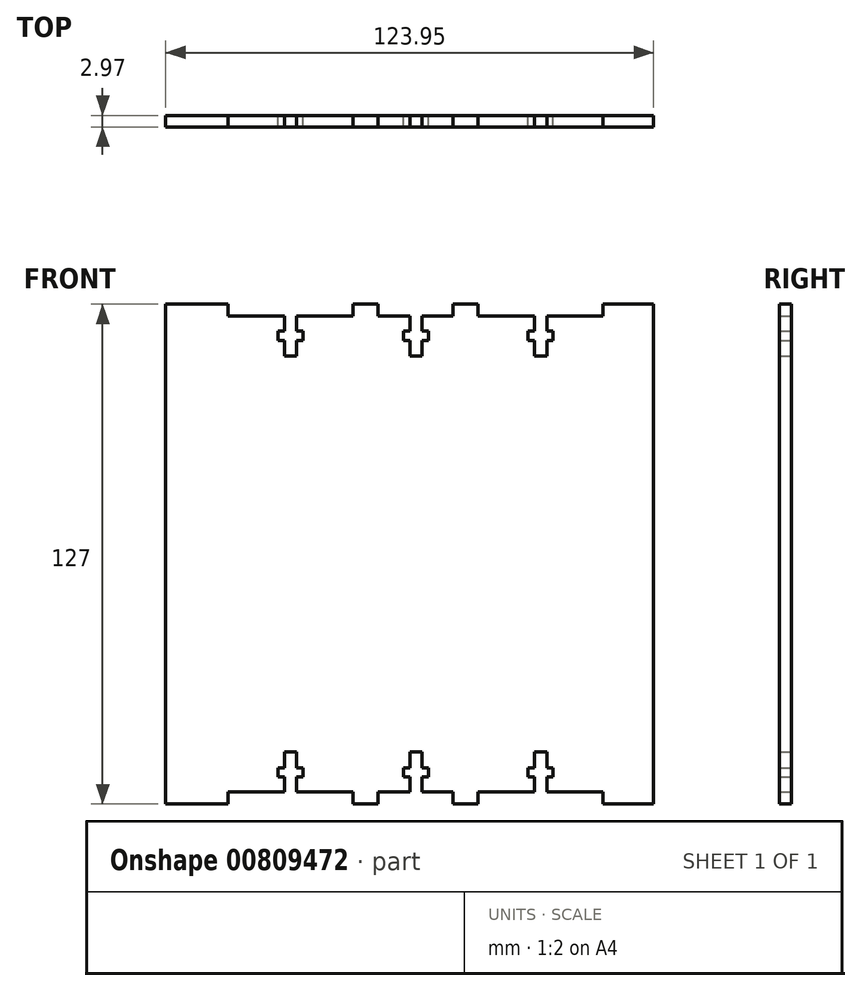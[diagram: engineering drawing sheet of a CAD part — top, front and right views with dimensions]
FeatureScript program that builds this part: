
annotation { "Feature Type Name" : "Feature", "Feature Type Description" : "" }
export const myFeature = defineFeature(function(context is Context, id is Id, definition is map)
    precondition{}
    {
        {
            var Q0;
            Q0=qCreatedBy(makeId("Front.planeOp"),FACE);
            var sketch = newSketch(context, id + "F0", { "sketchPlane" : qUnion([Q0])});
            skLineSegment(sketch, "E0.top", {"start": v(-63.5, -63.5) * mm, "end": v(-47.62, -63.5) * mm});
            skLineSegment(sketch, "E0.right", {"start": v(60.45, 0) * mm, "end": v(60.45, -63.5) * mm});
            skLineSegment(sketch, "E1", {"start": v(-60.45, 60.45) * mm, "end": v(-60.45, -67.28) * mm, "construction": true});
            skLineSegment(sketch, "E2", {"start": v(-66.3, -60.45) * mm, "end": v(-33.27, -60.45) * mm, "construction": true});
            skLineSegment(sketch, "E3", {"start": v(-47.62, -63.5) * mm, "end": v(-47.62, -60.45) * mm});
            skLineSegment(sketch, "E4", {"start": v(-15.88, -60.45) * mm, "end": v(-15.88, -63.5) * mm});
            skLineSegment(sketch, "E5", {"start": v(-9.53, -60.45) * mm, "end": v(-9.53, -63.5) * mm});
            skLineSegment(sketch, "E6.MirrorCS", {"start": v(9.53, -60.45) * mm, "end": v(9.53, -63.5) * mm});
            skLineSegment(sketch, "E7.MirrorCS", {"start": v(15.88, -60.45) * mm, "end": v(15.88, -63.5) * mm});
            skLineSegment(sketch, "E8.MirrorCS", {"start": v(47.62, -63.5) * mm, "end": v(47.62, -60.45) * mm});
            skLineSegment(sketch, "E9", {"start": v(-47.62, -60.45) * mm, "end": v(-33.27, -60.45) * mm});
            skLineSegment(sketch, "E10", {"start": v(-9.53, -60.45) * mm, "end": v(-1.44, -60.45) * mm});
            skLineSegment(sketch, "E11", {"start": v(15.88, -60.45) * mm, "end": v(30.16, -60.45) * mm});
            skLineSegment(sketch, "E12.trimOffspring", {"start": v(-15.88, -63.5) * mm, "end": v(-9.53, -63.5) * mm});
            skLineSegment(sketch, "E13.trimOffspring", {"start": v(-9.53, -60.45) * mm, "end": v(-1.44, -60.45) * mm, "construction": true});
            skLineSegment(sketch, "E14.trimOffspring", {"start": v(9.53, -63.5) * mm, "end": v(15.88, -63.5) * mm});
            skLineSegment(sketch, "E15.trimOffspring", {"start": v(47.62, -63.5) * mm, "end": v(60.45, -63.5) * mm});
            skLineSegment(sketch, "E16.trimOffspring", {"start": v(-63.5, -60.45) * mm, "end": v(-63.5, -63.5) * mm});
            skLineSegment(sketch, "E17", {"start": v(-63.5, -60.45) * mm, "end": v(-63.5, 0) * mm});
            skLineSegment(sketch, "E18", {"start": v(-63.5, 0) * mm, "end": v(60.45, 0) * mm});
            skLineSegment(sketch, "E19", {"start": v(-31.75, -61.85) * mm, "end": v(-31.75, 47.1) * mm, "construction": true});
            skLineSegment(sketch, "E20", {"start": v(31.75, -68.49) * mm, "end": v(31.75, 41.39) * mm, "construction": true});
            skLineSegment(sketch, "E21", {"start": v(-33.27, -60.45) * mm, "end": v(-33.27, -56.64) * mm});
            skLineSegment(sketch, "E22", {"start": v(-31.75, -50.3) * mm, "end": v(-33.27, -50.3) * mm});
            skLineSegment(sketch, "E23", {"start": v(-34.92, -54.26) * mm, "end": v(-34.92, -56.64) * mm});
            skLineSegment(sketch, "E24", {"start": v(-34.92, -56.64) * mm, "end": v(-33.27, -56.64) * mm});
            skLineSegment(sketch, "E25", {"start": v(-34.92, -54.26) * mm, "end": v(-33.27, -54.26) * mm});
            skLineSegment(sketch, "E26.trimOffspring", {"start": v(-33.27, -54.26) * mm, "end": v(-33.27, -50.3) * mm});
            skLineSegment(sketch, "E27.trimOffspring", {"start": v(-30.23, -60.45) * mm, "end": v(-15.88, -60.45) * mm, "construction": true});
            skLineSegment(sketch, "E28.trimOffspring", {"start": v(-30.23, -60.45) * mm, "end": v(-15.88, -60.45) * mm});
            skLineSegment(sketch, "E29.MirrorCS", {"start": v(-28.57, -54.26) * mm, "end": v(-30.23, -54.26) * mm});
            skLineSegment(sketch, "E30.MirrorCS", {"start": v(-28.57, -56.64) * mm, "end": v(-30.23, -56.64) * mm});
            skLineSegment(sketch, "E31.MirrorCS", {"start": v(-30.23, -60.45) * mm, "end": v(-30.23, -56.64) * mm});
            skLineSegment(sketch, "E32.MirrorCS", {"start": v(-30.23, -54.26) * mm, "end": v(-30.23, -50.3) * mm});
            skLineSegment(sketch, "E33.MirrorCS", {"start": v(-28.57, -54.26) * mm, "end": v(-28.57, -56.64) * mm});
            skLineSegment(sketch, "E34", {"start": v(-30.23, -50.3) * mm, "end": v(-31.75, -50.3) * mm});
            skLineSegment(sketch, "E35", {"start": v(-1.44, -60.45) * mm, "end": v(-1.44, -56.64) * mm});
            skLineSegment(sketch, "E36", {"start": v(0.09, -50.3) * mm, "end": v(-1.44, -50.3) * mm});
            skLineSegment(sketch, "E37", {"start": v(-3.09, -54.26) * mm, "end": v(-3.09, -56.64) * mm});
            skLineSegment(sketch, "E38", {"start": v(-3.09, -56.64) * mm, "end": v(-1.44, -56.64) * mm});
            skLineSegment(sketch, "E39", {"start": v(-3.09, -54.26) * mm, "end": v(-1.44, -54.26) * mm});
            skLineSegment(sketch, "E40.trimOffspring", {"start": v(-1.44, -54.26) * mm, "end": v(-1.44, -50.3) * mm});
            skLineSegment(sketch, "E41.MirrorCS", {"start": v(3.26, -54.26) * mm, "end": v(1.61, -54.26) * mm});
            skLineSegment(sketch, "E42.MirrorCS", {"start": v(3.26, -56.64) * mm, "end": v(1.61, -56.64) * mm});
            skLineSegment(sketch, "E43.MirrorCS", {"start": v(1.61, -60.45) * mm, "end": v(1.61, -56.64) * mm});
            skLineSegment(sketch, "E44.MirrorCS", {"start": v(1.61, -54.26) * mm, "end": v(1.61, -50.3) * mm});
            skLineSegment(sketch, "E45.MirrorCS", {"start": v(3.26, -54.26) * mm, "end": v(3.26, -56.64) * mm});
            skLineSegment(sketch, "E46", {"start": v(1.61, -50.3) * mm, "end": v(0.09, -50.3) * mm});
            skLineSegment(sketch, "E47.trimOffspring", {"start": v(1.61, -60.45) * mm, "end": v(30.16, -60.45) * mm, "construction": true});
            skLineSegment(sketch, "E48.trimOffspring", {"start": v(1.61, -60.45) * mm, "end": v(9.53, -60.45) * mm});
            skLineSegment(sketch, "E49", {"start": v(-34.92, -56.64) * mm, "end": v(30.16, -56.64) * mm, "construction": true});
            skLineSegment(sketch, "E50", {"start": v(-34.92, -54.26) * mm, "end": v(30.16, -54.26) * mm, "construction": true});
            skLineSegment(sketch, "E51", {"start": v(-33.27, -50.3) * mm, "end": v(50.65, -50.3) * mm, "construction": true});
            skLineSegment(sketch, "E52", {"start": v(30.16, -50.3) * mm, "end": v(30.16, -54.26) * mm});
            skLineSegment(sketch, "E53", {"start": v(30.16, -54.26) * mm, "end": v(28.58, -54.26) * mm});
            skLineSegment(sketch, "E54", {"start": v(28.58, -54.26) * mm, "end": v(28.58, -56.64) * mm});
            skLineSegment(sketch, "E55", {"start": v(28.57, -56.64) * mm, "end": v(30.16, -56.64) * mm});
            skLineSegment(sketch, "E56", {"start": v(30.16, -56.64) * mm, "end": v(30.16, -60.45) * mm});
            skLineSegment(sketch, "E57", {"start": v(31.75, -50.3) * mm, "end": v(30.16, -50.3) * mm});
            skLineSegment(sketch, "E58.MirrorCS", {"start": v(33.34, -54.26) * mm, "end": v(34.93, -54.26) * mm});
            skLineSegment(sketch, "E59.MirrorCS", {"start": v(34.93, -56.64) * mm, "end": v(33.34, -56.64) * mm});
            skLineSegment(sketch, "E60.MirrorCS", {"start": v(31.75, -50.3) * mm, "end": v(33.34, -50.3) * mm});
            skLineSegment(sketch, "E61.MirrorCS", {"start": v(33.34, -56.64) * mm, "end": v(33.34, -60.45) * mm});
            skLineSegment(sketch, "E62.MirrorCS", {"start": v(34.93, -54.26) * mm, "end": v(34.93, -56.64) * mm});
            skLineSegment(sketch, "E63.MirrorCS", {"start": v(33.34, -50.3) * mm, "end": v(33.34, -54.26) * mm});
            skLineSegment(sketch, "E64.trimOffspring", {"start": v(33.34, -60.45) * mm, "end": v(64.5, -60.45) * mm, "construction": true});
            skLineSegment(sketch, "E65.trimOffspring", {"start": v(33.34, -60.45) * mm, "end": v(47.62, -60.45) * mm});
            skLineSegment(sketch, "E66.trimOffspring", {"start": v(31.75, -56.64) * mm, "end": v(51.22, -56.64) * mm, "construction": true});
            skLineSegment(sketch, "E67.trimOffspring", {"start": v(33.34, -54.26) * mm, "end": v(50.65, -54.26) * mm, "construction": true});
            skLineSegment(sketch, "E68.MirrorCS", {"start": v(-34.93, 54.26) * mm, "end": v(-34.93, 56.64) * mm});
            skLineSegment(sketch, "E69.MirrorCS", {"start": v(-34.92, 56.64) * mm, "end": v(-33.27, 56.64) * mm});
            skLineSegment(sketch, "E70.MirrorCS", {"start": v(31.75, 50.3) * mm, "end": v(30.16, 50.3) * mm});
            skLineSegment(sketch, "E71.MirrorCS", {"start": v(3.26, 54.26) * mm, "end": v(1.61, 54.26) * mm});
            skLineSegment(sketch, "E72.MirrorCS", {"start": v(-34.92, 54.26) * mm, "end": v(-33.27, 54.26) * mm});
            skLineSegment(sketch, "E73.MirrorCS", {"start": v(28.57, 54.26) * mm, "end": v(28.57, 56.64) * mm});
            skLineSegment(sketch, "E74.MirrorCS", {"start": v(34.92, 56.64) * mm, "end": v(33.34, 56.64) * mm});
            skLineSegment(sketch, "E75.MirrorCS", {"start": v(33.34, 56.64) * mm, "end": v(33.34, 60.45) * mm});
            skLineSegment(sketch, "E76.MirrorCS", {"start": v(-33.27, 60.45) * mm, "end": v(-33.27, 56.64) * mm});
            skLineSegment(sketch, "E77.MirrorCS", {"start": v(30.16, 56.64) * mm, "end": v(30.16, 60.45) * mm});
            skLineSegment(sketch, "E78.MirrorCS", {"start": v(31.75, 50.3) * mm, "end": v(33.34, 50.3) * mm});
            skLineSegment(sketch, "E79.MirrorCS", {"start": v(-33.27, 54.26) * mm, "end": v(-33.27, 50.3) * mm});
            skLineSegment(sketch, "E80.MirrorCS", {"start": v(30.16, 50.3) * mm, "end": v(30.16, 54.26) * mm});
            skLineSegment(sketch, "E81.MirrorCS", {"start": v(-31.75, 50.3) * mm, "end": v(-33.27, 50.3) * mm});
            skLineSegment(sketch, "E82.MirrorCS", {"start": v(30.16, 54.26) * mm, "end": v(28.58, 54.26) * mm});
            skLineSegment(sketch, "E83.MirrorCS", {"start": v(33.34, 50.3) * mm, "end": v(33.34, 54.26) * mm});
            skLineSegment(sketch, "E84.MirrorCS", {"start": v(34.92, 54.26) * mm, "end": v(34.92, 56.64) * mm});
            skLineSegment(sketch, "E85.MirrorCS", {"start": v(33.34, 54.26) * mm, "end": v(34.92, 54.26) * mm});
            skLineSegment(sketch, "E86.MirrorCS", {"start": v(28.57, 56.64) * mm, "end": v(30.16, 56.64) * mm});
            skLineSegment(sketch, "E87.MirrorCS", {"start": v(-28.58, 54.26) * mm, "end": v(-28.58, 56.64) * mm});
            skLineSegment(sketch, "E88.MirrorCS", {"start": v(-3.09, 56.64) * mm, "end": v(-1.44, 56.64) * mm});
            skLineSegment(sketch, "E89.MirrorCS", {"start": v(1.61, 60.45) * mm, "end": v(1.61, 56.64) * mm});
            skLineSegment(sketch, "E90.MirrorCS", {"start": v(3.26, 54.26) * mm, "end": v(3.26, 56.64) * mm});
            skLineSegment(sketch, "E91.MirrorCS", {"start": v(-30.23, 60.45) * mm, "end": v(-30.23, 56.64) * mm});
            skLineSegment(sketch, "E92.MirrorCS", {"start": v(-28.58, 56.64) * mm, "end": v(-30.23, 56.64) * mm});
            skLineSegment(sketch, "E93.MirrorCS", {"start": v(-30.23, 50.3) * mm, "end": v(-31.75, 50.3) * mm});
            skLineSegment(sketch, "E94.MirrorCS", {"start": v(-9.53, 60.45) * mm, "end": v(-9.53, 63.5) * mm});
            skLineSegment(sketch, "E95.MirrorCS", {"start": v(9.53, 60.45) * mm, "end": v(9.53, 63.5) * mm});
            skLineSegment(sketch, "E96.MirrorCS", {"start": v(-3.09, 54.26) * mm, "end": v(-3.09, 56.64) * mm});
            skLineSegment(sketch, "E97.MirrorCS", {"start": v(3.26, 56.64) * mm, "end": v(1.61, 56.64) * mm});
            skLineSegment(sketch, "E98.MirrorCS", {"start": v(-3.09, 54.26) * mm, "end": v(-1.44, 54.26) * mm});
            skLineSegment(sketch, "E99.MirrorCS", {"start": v(-28.58, 54.26) * mm, "end": v(-30.23, 54.26) * mm});
            skLineSegment(sketch, "E100.MirrorCS", {"start": v(-1.44, 60.45) * mm, "end": v(-1.44, 56.64) * mm});
            skLineSegment(sketch, "E101.MirrorCS", {"start": v(1.61, 54.26) * mm, "end": v(1.61, 50.3) * mm});
            skLineSegment(sketch, "E102.MirrorCS", {"start": v(15.88, 60.45) * mm, "end": v(15.88, 63.5) * mm});
            skLineSegment(sketch, "E103.MirrorCS", {"start": v(-30.23, 54.26) * mm, "end": v(-30.23, 50.3) * mm});
            skLineSegment(sketch, "E104.MirrorCS", {"start": v(-1.44, 54.26) * mm, "end": v(-1.44, 50.3) * mm});
            skLineSegment(sketch, "E105.MirrorCS", {"start": v(-47.63, 63.5) * mm, "end": v(-47.63, 60.45) * mm});
            skLineSegment(sketch, "E106.MirrorCS", {"start": v(47.62, 63.5) * mm, "end": v(47.62, 60.45) * mm});
            skLineSegment(sketch, "E107.MirrorCS", {"start": v(1.61, 50.3) * mm, "end": v(0.09, 50.3) * mm});
            skLineSegment(sketch, "E108.MirrorCS", {"start": v(-63.5, 60.45) * mm, "end": v(-63.5, 63.5) * mm});
            skLineSegment(sketch, "E109.MirrorCS", {"start": v(-15.88, 60.45) * mm, "end": v(-15.88, 63.5) * mm});
            skLineSegment(sketch, "E110.MirrorCS", {"start": v(0.09, 50.3) * mm, "end": v(-1.44, 50.3) * mm});
            skLineSegment(sketch, "E111.MirrorCS", {"start": v(33.34, 60.45) * mm, "end": v(47.62, 60.45) * mm});
            skLineSegment(sketch, "E112.MirrorCS", {"start": v(1.61, 60.45) * mm, "end": v(9.53, 60.45) * mm});
            skLineSegment(sketch, "E113.MirrorCS", {"start": v(15.88, 60.45) * mm, "end": v(30.16, 60.45) * mm});
            skLineSegment(sketch, "E114.MirrorCS", {"start": v(-9.53, 60.45) * mm, "end": v(-1.44, 60.45) * mm});
            skLineSegment(sketch, "E115.MirrorCS", {"start": v(-47.62, 60.45) * mm, "end": v(-33.27, 60.45) * mm});
            skLineSegment(sketch, "E116.MirrorCS", {"start": v(-30.23, 60.45) * mm, "end": v(-15.88, 60.45) * mm});
            skLineSegment(sketch, "E117.MirrorCS", {"start": v(-34.92, 56.64) * mm, "end": v(30.16, 56.64) * mm, "construction": true});
            skLineSegment(sketch, "E118.MirrorCS", {"start": v(-66.3, 60.45) * mm, "end": v(-33.27, 60.45) * mm, "construction": true});
            skLineSegment(sketch, "E119.MirrorCS", {"start": v(60.45, 0) * mm, "end": v(60.45, 63.5) * mm});
            skLineSegment(sketch, "E120.MirrorCS", {"start": v(-63.5, 63.5) * mm, "end": v(-47.63, 63.5) * mm});
            skLineSegment(sketch, "E121.MirrorCS", {"start": v(9.52, 63.5) * mm, "end": v(15.87, 63.5) * mm});
            skLineSegment(sketch, "E122.MirrorCS", {"start": v(-30.23, 60.45) * mm, "end": v(-15.88, 60.45) * mm, "construction": true});
            skLineSegment(sketch, "E123.MirrorCS", {"start": v(-9.53, 60.45) * mm, "end": v(-1.44, 60.45) * mm, "construction": true});
            skLineSegment(sketch, "E124.MirrorCS", {"start": v(-63.5, 60.45) * mm, "end": v(-63.5, 0) * mm});
            skLineSegment(sketch, "E125.MirrorCS", {"start": v(33.34, 54.26) * mm, "end": v(50.65, 54.26) * mm, "construction": true});
            skLineSegment(sketch, "E126.MirrorCS", {"start": v(33.34, 60.45) * mm, "end": v(64.5, 60.45) * mm, "construction": true});
            skLineSegment(sketch, "E127.MirrorCS", {"start": v(1.61, 60.45) * mm, "end": v(30.16, 60.45) * mm, "construction": true});
            skLineSegment(sketch, "E128.MirrorCS", {"start": v(31.75, 56.64) * mm, "end": v(51.22, 56.64) * mm, "construction": true});
            skLineSegment(sketch, "E129.MirrorCS", {"start": v(47.63, 63.5) * mm, "end": v(60.45, 63.5) * mm});
            skLineSegment(sketch, "E130.MirrorCS", {"start": v(-33.27, 50.3) * mm, "end": v(50.65, 50.3) * mm, "construction": true});
            skLineSegment(sketch, "E131.MirrorCS", {"start": v(-15.87, 63.5) * mm, "end": v(-9.52, 63.5) * mm});
            skLineSegment(sketch, "E132.MirrorCS", {"start": v(-34.92, 54.26) * mm, "end": v(30.16, 54.26) * mm, "construction": true});
            skSolve(sketch);
        }
        {
            var Q0;
            Q0 = qSketchRegion(id + "F0", true);
            extrude(context, id + "F1", {"entities" : qUnion([Q0]), "depth" : 2.97 * mm, "offsetDistance" : 25.4 * mm});
        }
    });
